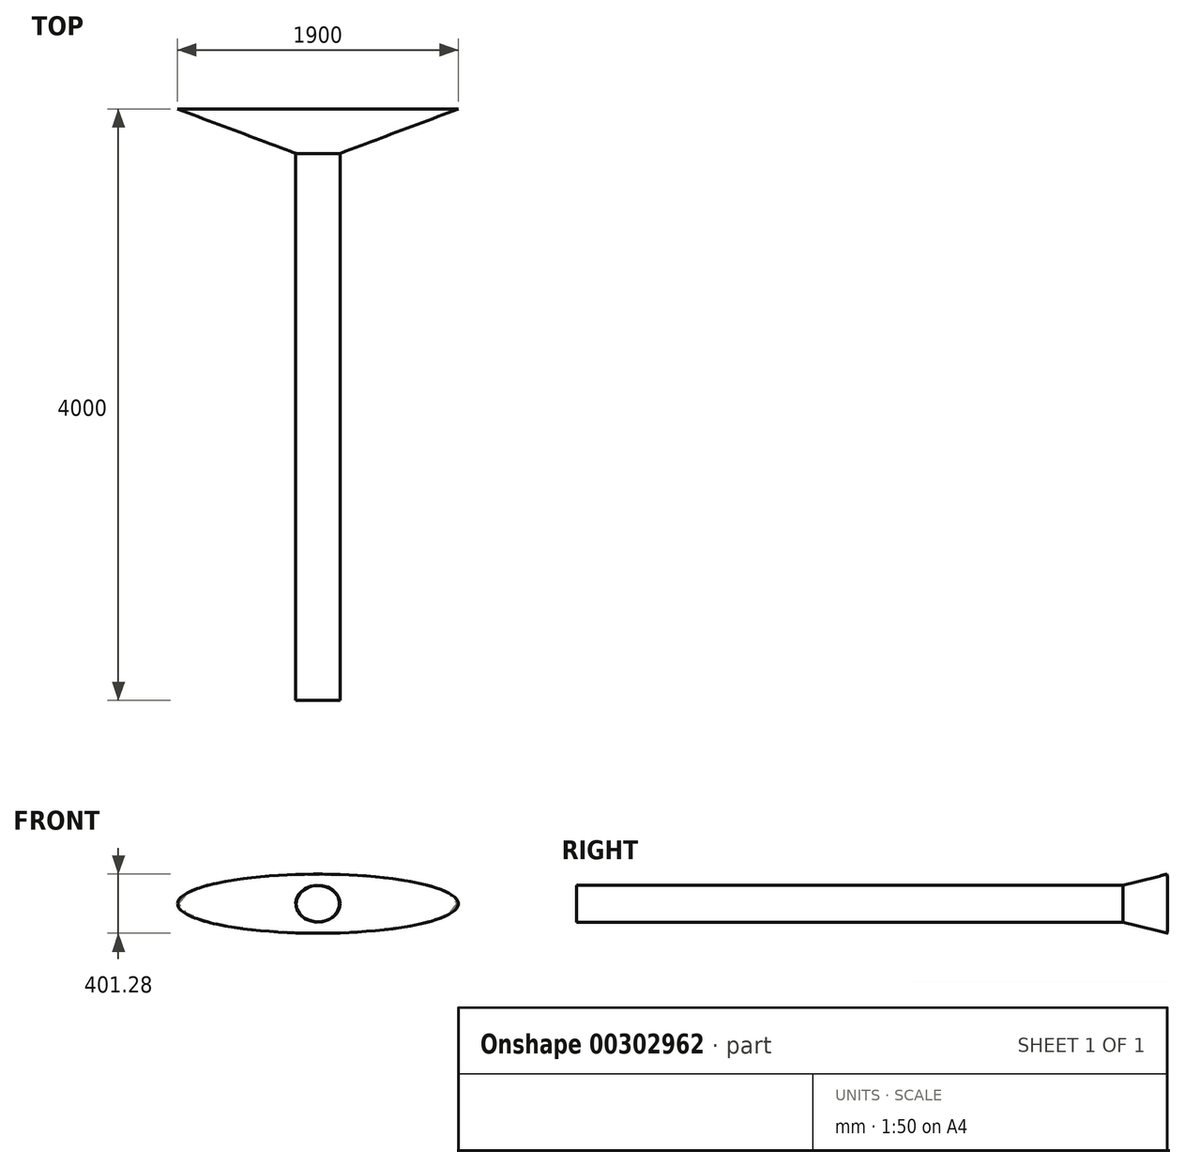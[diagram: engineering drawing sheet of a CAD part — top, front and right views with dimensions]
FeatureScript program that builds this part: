
annotation { "Feature Type Name" : "Feature", "Feature Type Description" : "" }
export const myFeature = defineFeature(function(context is Context, id is Id, definition is map)
    precondition{}
    {
        {
            var Q0;
            Q0=qCreatedBy(makeId("Front.planeOp"),FACE);
            var sketch = newSketch(context, id + "F0", { "sketchPlane" : qUnion([Q0])});
            skEllipse(sketch, "E0", {"center": v(0, 0) * mm, "majorRadius": 150 * mm, "minorRadius": 125 * mm, "majorAxis": v(1, 0)});
            skSolve(sketch);
        }
        {
            var Q0;
            Q0=qCreatedBy(makeId("Front.planeOp"),FACE);
            cPlane(context, id + "F1", {"entities" : qUnion([Q0]), "cplaneType" : CPlaneType.OFFSET, "offset" : 4000 * mm, "oppositeDirection" : true, "width" : 150 * mm, "height" : 150 * mm});
        }
        {
            var Q0;
            Q0=qCreatedBy(id+"F1.planeOp",FACE);
            var sketch = newSketch(context, id + "F2", { "sketchPlane" : qUnion([Q0])});
            skEllipse(sketch, "E1", {"center": v(0, 0) * mm, "majorRadius": 950 * mm, "minorRadius": 200 * mm, "majorAxis": v(-1, 0)});
            skSolve(sketch);
        }
        {
            var Q0;
            Q0=qCreatedBy(makeId("Front.planeOp"),FACE);
            cPlane(context, id + "F3", {"entities" : qUnion([Q0]), "cplaneType" : CPlaneType.OFFSET, "offset" : 3700 * mm, "oppositeDirection" : true, "width" : 150 * mm, "height" : 150 * mm});
        }
        {
            var Q0;
            Q0=qCreatedBy(id+"F3.planeOp",FACE);
            var sketch = newSketch(context, id + "F4", { "sketchPlane" : qUnion([Q0])});
            skEllipse(sketch, "E2.0", {"center": v(0, 0) * mm, "majorRadius": 150 * mm, "minorRadius": 125 * mm, "majorAxis": v(1, 0)});
            skSolve(sketch);
        }
        {
            var Q0;
            Q0=makeQuery(id+"F4.imprint","IMPRINT",FACE,{"disambiguationData":[TD([[makeQuery(id+"F4.imprint","IMPRINT",EDGE,{"derivedFrom":sQuery(id+"F4.wireOp",EDGE,"E2.0")}),1.0]])]});
            var Q1;
            Q1=makeQuery(id+"F0.imprint","IMPRINT",FACE,{"disambiguationData":[TD([[makeQuery(id+"F0.imprint","IMPRINT",EDGE,{"derivedFrom":sQuery(id+"F0.wireOp",EDGE,"E0")}),1.0]])]});
            loft(context, id + "F5", {"sheetProfilesArray" : [{ "sheetProfileEntities" : qUnion([Q0]) }, { "sheetProfileEntities" : qUnion([Q1]) }]});
        }
        {
            var Q1;
            Q1=makeQuery(id+"F2.imprint","IMPRINT",FACE,{"disambiguationData":[TD([[makeQuery(id+"F2.imprint","IMPRINT",EDGE,{"derivedFrom":sQuery(id+"F2.wireOp",EDGE,"E1")}),1.0]])]});
            var Q2;
            Q2=makeQuery(id+"F5.opLoft","CAP_FACE",FACE,{"disambiguationData":[OSD([makeQuery(id+"F4.imprint","IMPRINT",FACE,{"disambiguationData":[TD([[makeQuery(id+"F4.imprint","IMPRINT",EDGE,{"derivedFrom":sQuery(id+"F4.wireOp",EDGE,"E2.0")}),1.0]])]})])],"isStart":true});
            loft(context, id + "F6", {"operationType" : NewBodyOperationType.ADD, "sheetProfilesArray" : [{ "sheetProfileEntities" : qUnion([Q1]) }, { "sheetProfileEntities" : qUnion([Q2]) }]});
        }
        {
            var Q0;
            Q0=makeQuery(id+"F6.opLoft","CAP_FACE",FACE,{"disambiguationData":[OSD([makeQuery(id+"F2.imprint","IMPRINT",FACE,{"disambiguationData":[TD([[makeQuery(id+"F2.imprint","IMPRINT",EDGE,{"derivedFrom":sQuery(id+"F2.wireOp",EDGE,"E1")}),1.0]])]})])],"isStart":true});
            var Q1;
            Q1=makeQuery(id+"F5.opLoft","CAP_FACE",FACE,{"disambiguationData":[OSD([makeQuery(id+"F0.imprint","IMPRINT",FACE,{"disambiguationData":[TD([[makeQuery(id+"F0.imprint","IMPRINT",EDGE,{"derivedFrom":sQuery(id+"F0.wireOp",EDGE,"E0")}),1.0]])]})])],"isStart":true});
            shell(context, id + "F7", {"entities" : qUnion([Q0, Q1]), "thickness" : 2.5 * mm});
        }
        {
            var Q0;
            Q0=makeQuery(id+"F7.opShell","OFFSET_EDGE",EDGE,{"disambiguationData":[OSD([sQuery(id+"F2.wireOp",EDGE,"E1"),sQuery(id+"F4.wireOp",EDGE,"E2.0")])]});
            fillet(context, id + "F8", {"entities" : qUnion([Q0]), "radius" : 5 * mm, "tangentPropagation" : true, "allowEdgeOverflow" : false});
        }
    });
